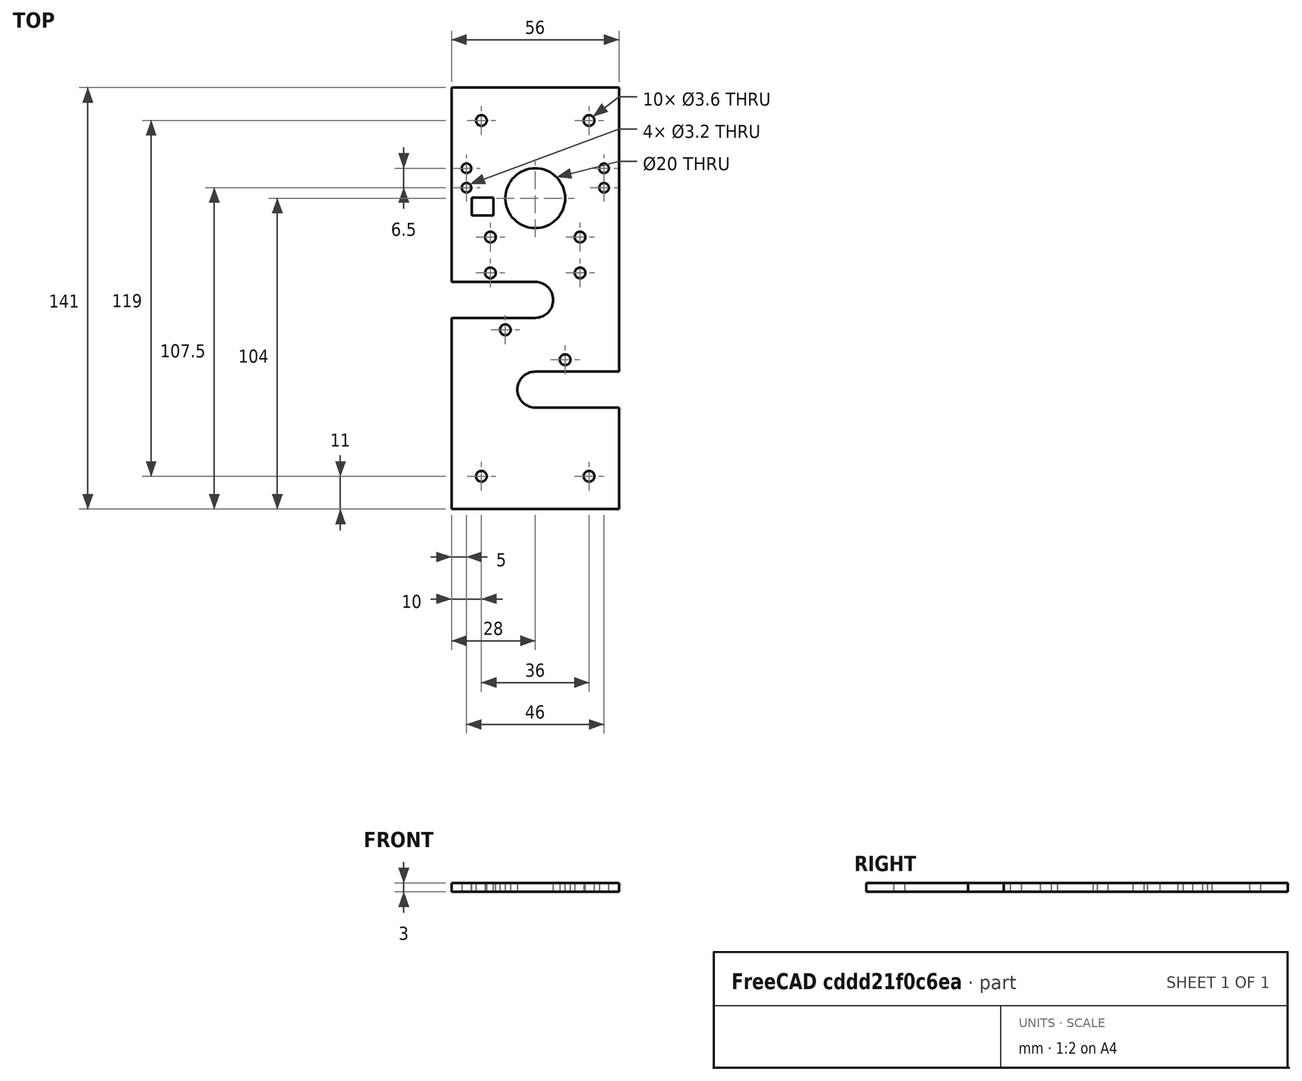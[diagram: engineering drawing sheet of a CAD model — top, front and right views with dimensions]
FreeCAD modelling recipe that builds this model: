
FCSTD DOCUMENT  (FreeCAD 0.16R6706 (Git))
Label: Plate Extrusora
License: All rights reserved
LicenseURL: http://en.wikipedia.org/wiki/All_rights_reserved
objects: Path::FeaturePython×19, Sketcher::SketchObject×1, PartDesign::Pad×1, Path::FeatureCompoundPython×1
note: 3 computed .brp shape members not serialized (recipe doc carries the construction recipe); baked Part::Feature solids carry a one-line shape summary decoded from their .brp

FEATURE [Sketcher::SketchObject] Sketch
  sketch-geometry (40):
    g0: LineSegment StartX=-28 StartY=141 StartZ=0 EndX=28 EndY=141 EndZ=0
    g1: LineSegment StartX=28 StartY=141 StartZ=0 EndX=28 EndY=46 EndZ=0
    g2: LineSegment StartX=28 StartY=0 StartZ=0 EndX=-28 EndY=0 EndZ=0
    g3: LineSegment StartX=-28 StartY=0 StartZ=0 EndX=-28 EndY=64 EndZ=0
    g4: ArcOfCircle CenterX=0 CenterY=70 CenterZ=0 NormalX=0 NormalY=0 NormalZ=1 Radius=6 StartAngle=4.71239 EndAngle=7.85398
    g5: ArcOfCircle CenterX=-1e-12 CenterY=40 CenterZ=0 NormalX=0 NormalY=0 NormalZ=1 Radius=6 StartAngle=1.5708 EndAngle=4.71239
    g6: Circle CenterX=0 CenterY=104 CenterZ=0 NormalX=0 NormalY=0 NormalZ=1 Radius=10
    g7: LineSegment [constr] StartX=-18 StartY=130 StartZ=0 EndX=18 EndY=130 EndZ=0
    g8: Circle CenterX=-18 CenterY=130 CenterZ=0 NormalX=0 NormalY=0 NormalZ=1 Radius=1.8
    g9: Circle CenterX=18 CenterY=130 CenterZ=0 NormalX=0 NormalY=0 NormalZ=1 Radius=1.8
    g10: LineSegment [constr] StartX=-18 StartY=11 StartZ=0 EndX=18 EndY=11 EndZ=0
    g11: Circle CenterX=-18 CenterY=11 CenterZ=0 NormalX=0 NormalY=0 NormalZ=1 Radius=1.8
    g12: Circle CenterX=18 CenterY=11 CenterZ=0 NormalX=0 NormalY=0 NormalZ=1 Radius=1.8
    g13: LineSegment [constr] StartX=-23 StartY=114 StartZ=0 EndX=-23 EndY=107.5 EndZ=0
    g14: Circle CenterX=-23 CenterY=114 CenterZ=0 NormalX=0 NormalY=0 NormalZ=1 Radius=1.6
    g15: Circle CenterX=-23 CenterY=107.5 CenterZ=0 NormalX=0 NormalY=0 NormalZ=1 Radius=1.6
    g16: LineSegment [constr] StartX=23 StartY=114 StartZ=0 EndX=23 EndY=107.5 EndZ=0
    g17: Circle CenterX=23 CenterY=114 CenterZ=0 NormalX=0 NormalY=0 NormalZ=1 Radius=1.6
    g18: Circle CenterX=23 CenterY=107.5 CenterZ=0 NormalX=0 NormalY=0 NormalZ=1 Radius=1.6
    g19: LineSegment [constr] StartX=-24.7268 StartY=119 StartZ=0 EndX=33.9548 EndY=119 EndZ=0
    g20: LineSegment [constr] StartX=-27.9869 StartY=22 StartZ=0 EndX=33.2236 EndY=22 EndZ=0
    g21: LineSegment StartX=-21.2321 StartY=104.225 StartZ=0 EndX=-13.9434 EndY=104.225 EndZ=0
    g22: LineSegment StartX=-13.9434 StartY=104.225 StartZ=0 EndX=-13.9434 EndY=98.2464 EndZ=0
    g23: LineSegment StartX=-13.9434 StartY=98.2464 StartZ=0 EndX=-21.2321 EndY=98.2464 EndZ=0
    g24: LineSegment StartX=-21.2321 StartY=98.2464 StartZ=0 EndX=-21.2321 EndY=104.225 EndZ=0
    g25: LineSegment [constr] StartX=-15 StartY=85 StartZ=0 EndX=15 EndY=85 EndZ=0
    g26: LineSegment StartX=2e-12 StartY=64 StartZ=0 EndX=-28 EndY=64 EndZ=0
    g27: LineSegment StartX=-28 StartY=76 StartZ=0 EndX=3e-12 EndY=76 EndZ=0
    g28: LineSegment StartX=-2e-12 StartY=46 StartZ=0 EndX=28 EndY=46 EndZ=0
    g29: LineSegment StartX=28 StartY=34 StartZ=0 EndX=1e-12 EndY=34 EndZ=0
    g30: LineSegment StartX=28 StartY=34 StartZ=0 EndX=28 EndY=0 EndZ=0
    g31: LineSegment StartX=-28 StartY=76 StartZ=0 EndX=-28 EndY=141 EndZ=0
    g32: Circle CenterX=-10 CenterY=60 CenterZ=0 NormalX=0 NormalY=0 NormalZ=1 Radius=1.8
    g33: Circle CenterX=10 CenterY=50 CenterZ=0 NormalX=0 NormalY=0 NormalZ=1 Radius=1.8
    g34: LineSegment [constr] StartX=-15 StartY=91 StartZ=0 EndX=-15 EndY=79 EndZ=0
    g35: Circle CenterX=-15 CenterY=91 CenterZ=0 NormalX=0 NormalY=0 NormalZ=1 Radius=1.8
    g36: Circle CenterX=-15 CenterY=79 CenterZ=0 NormalX=0 NormalY=0 NormalZ=1 Radius=1.8
    g37: LineSegment [constr] StartX=15 StartY=91 StartZ=0 EndX=15 EndY=79 EndZ=0
    g38: Circle CenterX=15 CenterY=91 CenterZ=0 NormalX=0 NormalY=0 NormalZ=1 Radius=1.8
    g39: Circle CenterX=15 CenterY=79 CenterZ=0 NormalX=0 NormalY=0 NormalZ=1 Radius=1.8
  constraints (109):
    c: Coincident(g0,g1)
    c: Coincident(g30,g2)
    c: Coincident(g2,g3)
    c: Coincident(g31,g0)
    c: Horizontal(g0)
    c: Horizontal(g2)
    c: Vertical(g1)
    c: Vertical(g3)
    c: DistanceY(g30,g1) = 141
    c: DistanceX(g0,g0) = 56
    c: Radius(g6) = 10
    c: Radius(g5) = 6
    c: Equal(g5,g4)
    c: DistanceY(g-1,g5) = 40
    c: DistanceY(g5,g4) = 30
    c: DistanceY(g6,g0) = 37
    c: Horizontal(g7)
    c: DistanceX(g7,g7) = 36
    c: Radius(g8) = 1.8
    c: Equal(g8,g9) = 1.8
    c: Coincident(g7,g8)
    c: Coincident(g7,g9)
    c: DistanceY(g7,g0) = 11
    c: Horizontal(g10)
    c: Equal(g7,g10) = 25
    c: Equal(g8,g11) = 1.8
    c: Equal(g11,g12) = 1.8
    c: Coincident(g10,g12)
    c: DistanceY(g-1,g10) = 11
    c: DistanceY(g13,g13) = 6.5
    c: Vertical(g13)
    c: Radius(g14) = 1.6
    c: Equal(g14,g15) = 1.6
    c: Coincident(g14,g13)
    c: Coincident(g15,g13)
    c: Equal(g13,g16) = 6.5
    c: Vertical(g16)
    c: Equal(g14,g17) = 1.6
    c: Equal(g17,g18) = 1.6
    c: Coincident(g17,g16)
    c: Coincident(g18,g16)
    c: DistanceX(g0,g13) = 5
    c: DistanceX(g16,g0) = 5
    c: Horizontal(g19)
    c: DistanceY(g19,g0) = 22
    c: Symmetric(g30,g2,g-1)
    c: PointOnObject(g6,g-2)
    c: Horizontal(g20)
    c: DistanceY(g30,g20) = 22
    c: Coincident(g21,g22)
    c: Coincident(g22,g23)
    c: Coincident(g23,g24)
    c: Coincident(g24,g21)
    c: Horizontal(g21)
    c: Horizontal(g23)
    c: Vertical(g22)
    c: Vertical(g24)
    c: DistanceY(g16,g19) = 5
    c: DistanceY(g13,g19) = 5
    c: Horizontal(g25)
    c: Symmetric(g25,g25,g-2)
    c: DistanceX(g25,g25) = 30
    c: DistanceY(g25,g6) = 19
    c: DistanceY(g4,g25) = 15
    c: Horizontal(g26)
    c: Horizontal(g27)
    c: Horizontal(g28)
    c: Horizontal(g29)
    c: Coincident(g5,g28)
    c: Coincident(g5,g29)
    c: Tangent(g1,g30)
    c: Coincident(g28,g1)
    c: Coincident(g29,g30)
    c: Symmetric(g26,g27,g4)
    c: Tangent(g3,g31)
    c: Coincident(g27,g31)
    c: Coincident(g26,g3)
    c: Equal(g8,g32) = 1.8
    c: Equal(g8,g33) = 1.8
    c: DistanceX(g5,g33) = 10
    c: DistanceY(g5,g33) = 10
    c: DistanceX(g32,g4) = 10
    c: DistanceY(g32,g4) = 10
    c: Coincident(g4,g27)
    c: Vertical(g34)
    c: DistanceY(g34,g34) = 12
    c: Radius(g35) = 1.8
    c: Equal(g35,g36) = 1.8
    c: Coincident(g34,g35)
    c: Coincident(g34,g36)
    c: Vertical(g37)
    c: Equal(g34,g37) = 15
    c: Equal(g35,g38) = 1.8
    c: Equal(g38,g39) = 1.8
    c: Coincident(g37,g38)
    c: Coincident(g37,g39)
    c: Symmetric(g37,g37,g25)
    c: Symmetric(g34,g34,g25)
    c: DistanceX(g28,g28) = 28
    c: Equal(g28,g26)
    c: Coincident(g4,g26)
    c: DistanceY(g25,g7) = 45
    c: Equal(g28,g29)
    c: Equal(g29,g26)
    c: Equal(g26,g27)
    c: Angle(g5) = 3.14159
    c: Symmetric(g7,g7,g-2)
    c: Coincident(g11,g10)
    c: Symmetric(g10,g10,g-2)
FEATURE [PartDesign::Pad] Pad
  Length = 3
  Length2 = 100
  Sketch = -> Sketch
  Type = 0
FEATURE [Path::FeaturePython] Machine  label="Machine_"  # Path/CAM operation (typed FeaturePython)
  MachineUnits = 0
  X = 0
  X_Max = 0
  X_Min = 0
  Y = 0
  Y_Max = 0
  Y_Min = 0
  Z = 0
  Z_Max = 0
  Z_Min = 0
FEATURE [Path::FeaturePython] Tool  label="Tool1"  # Path/CAM operation (typed FeaturePython)
  SpindleDir = 0
  SpindleSpeed = 0
  ToolNumber = 1
FEATURE [Path::FeaturePython] Profile  label="Berco"  # Path/CAM operation (typed FeaturePython)
  Active = true
  Base = -> Pad
  ClearanceHeight = 3
  Direction = 1
  Edge1 = -> Pad [Edge81]
  EndPoint = (0,0,0)
  ExtendAtEnd = 0
  ExtendAtStart = 0
  FinalDepth = -3.5
  HorizFeed = 127
  LeadInLineLen = 0
  LeadOutLineLen = 0
  OffsetExtra = 0
  PathClosed = true
  RetractHeight = 0
  RollRadius = 0
  SegLen = 0.5
  Side = 1
  StartDepth = 0
  StartPoint = (0,0,0)
  StepDown = 3.5
  ToolNumber = 1
  UseEndPoint = false
  UsePlacements = false
  UseStartDepth = true
  UseStartPoint = false
  VertFeed = 127
FEATURE [Path::FeaturePython] Profile001  label="Berco001"  # Path/CAM operation (typed FeaturePython)
  Active = true
  Base = -> Pad
  ClearanceHeight = 3
  Direction = 1
  Edge1 = -> Pad [Edge78]
  EndPoint = (0,0,0)
  ExtendAtEnd = 0
  ExtendAtStart = 0
  FinalDepth = -3.5
  HorizFeed = 127
  LeadInLineLen = 0
  LeadOutLineLen = 0
  OffsetExtra = 0
  PathClosed = true
  RetractHeight = 0
  RollRadius = 0
  SegLen = 0.5
  Side = 1
  StartDepth = 0
  StartPoint = (0,0,0)
  StepDown = 3.5
  ToolNumber = 1
  UseEndPoint = false
  UsePlacements = false
  UseStartDepth = true
  UseStartPoint = false
  VertFeed = 127
FEATURE [Path::FeaturePython] Profile002  label="Berco002"  # Path/CAM operation (typed FeaturePython)
  Active = true
  Base = -> Pad
  ClearanceHeight = 3
  Direction = 1
  Edge1 = -> Pad [Edge75]
  EndPoint = (0,0,0)
  ExtendAtEnd = 0
  ExtendAtStart = 0
  FinalDepth = -3.5
  HorizFeed = 127
  LeadInLineLen = 0
  LeadOutLineLen = 0
  OffsetExtra = 0
  PathClosed = true
  RetractHeight = 0
  RollRadius = 0
  SegLen = 0.5
  Side = 1
  StartDepth = 0
  StartPoint = (0,0,0)
  StepDown = 3.5
  ToolNumber = 1
  UseEndPoint = false
  UsePlacements = false
  UseStartDepth = true
  UseStartPoint = false
  VertFeed = 127
FEATURE [Path::FeaturePython] Profile003  label="Berco003"  # Path/CAM operation (typed FeaturePython)
  Active = true
  Base = -> Pad
  ClearanceHeight = 3
  Direction = 1
  Edge1 = -> Pad [Edge72]
  EndPoint = (0,0,0)
  ExtendAtEnd = 0
  ExtendAtStart = 0
  FinalDepth = -3.5
  HorizFeed = 127
  LeadInLineLen = 0
  LeadOutLineLen = 0
  OffsetExtra = 0
  PathClosed = true
  RetractHeight = 0
  RollRadius = 0
  SegLen = 0.5
  Side = 1
  StartDepth = 0
  StartPoint = (0,0,0)
  StepDown = 3.5
  ToolNumber = 1
  UseEndPoint = false
  UsePlacements = false
  UseStartDepth = true
  UseStartPoint = false
  VertFeed = 127
FEATURE [Path::FeaturePython] Profile004  label="Enforcador"  # Path/CAM operation (typed FeaturePython)
  Active = true
  Base = -> Pad
  ClearanceHeight = 3
  Direction = 1
  Edge1 = -> Pad [Edge69]
  EndPoint = (0,0,0)
  ExtendAtEnd = 0
  ExtendAtStart = 0
  FinalDepth = -3.5
  HorizFeed = 127
  LeadInLineLen = 0
  LeadOutLineLen = 0
  OffsetExtra = 0
  PathClosed = true
  RetractHeight = 0
  RollRadius = 0
  SegLen = 0.5
  Side = 1
  StartDepth = 0
  StartPoint = (0,0,0)
  StepDown = 3.5
  ToolNumber = 1
  UseEndPoint = false
  UsePlacements = false
  UseStartDepth = true
  UseStartPoint = false
  VertFeed = 127
FEATURE [Path::FeaturePython] Profile005  label="Enforcador001"  # Path/CAM operation (typed FeaturePython)
  Active = true
  Base = -> Pad
  ClearanceHeight = 3
  Direction = 1
  Edge1 = -> Pad [Edge66]
  EndPoint = (0,0,0)
  ExtendAtEnd = 0
  ExtendAtStart = 0
  FinalDepth = -3.5
  HorizFeed = 127
  LeadInLineLen = 0
  LeadOutLineLen = 0
  OffsetExtra = 0
  PathClosed = true
  RetractHeight = 0
  RollRadius = 0
  SegLen = 0.5
  Side = 1
  StartDepth = 0
  StartPoint = (0,0,0)
  StepDown = 3.5
  ToolNumber = 1
  UseEndPoint = false
  UsePlacements = false
  UseStartDepth = true
  UseStartPoint = false
  VertFeed = 127
FEATURE [Path::FeaturePython] Profile006  label="presilha correia"  # Path/CAM operation (typed FeaturePython)
  Active = true
  Base = -> Pad
  ClearanceHeight = 3
  Direction = 1
  Edge1 = -> Pad [Edge60]
  EndPoint = (0,0,0)
  ExtendAtEnd = 0
  ExtendAtStart = 0
  FinalDepth = -3.5
  HorizFeed = 127
  LeadInLineLen = 0
  LeadOutLineLen = 0
  OffsetExtra = 0
  PathClosed = true
  RetractHeight = 0
  RollRadius = 0
  SegLen = 0.5
  Side = 1
  StartDepth = 0
  StartPoint = (0,0,0)
  StepDown = 3.5
  ToolNumber = 1
  UseEndPoint = false
  UsePlacements = false
  UseStartDepth = true
  UseStartPoint = false
  VertFeed = 127
FEATURE [Path::FeaturePython] Profile007  label="presilha correia001"  # Path/CAM operation (typed FeaturePython)
  Active = true
  Base = -> Pad
  ClearanceHeight = 3
  Direction = 1
  Edge1 = -> Pad [Edge63]
  EndPoint = (0,0,0)
  ExtendAtEnd = 0
  ExtendAtStart = 0
  FinalDepth = -3.5
  HorizFeed = 127
  LeadInLineLen = 0
  LeadOutLineLen = 0
  OffsetExtra = 0
  PathClosed = true
  RetractHeight = 0
  RollRadius = 0
  SegLen = 0.5
  Side = 1
  StartDepth = 0
  StartPoint = (0,0,0)
  StepDown = 3.5
  ToolNumber = 1
  UseEndPoint = false
  UsePlacements = false
  UseStartDepth = true
  UseStartPoint = false
  VertFeed = 127
FEATURE [Path::FeaturePython] Profile008  label="presilha correia002"  # Path/CAM operation (typed FeaturePython)
  Active = true
  Base = -> Pad
  ClearanceHeight = 3
  Direction = 1
  Edge1 = -> Pad [Edge54]
  EndPoint = (0,0,0)
  ExtendAtEnd = 0
  ExtendAtStart = 0
  FinalDepth = -3.5
  HorizFeed = 127
  LeadInLineLen = 0
  LeadOutLineLen = 0
  OffsetExtra = 0
  PathClosed = true
  RetractHeight = 0
  RollRadius = 0
  SegLen = 0.5
  Side = 1
  StartDepth = 0
  StartPoint = (0,0,0)
  StepDown = 3.5
  ToolNumber = 1
  UseEndPoint = false
  UsePlacements = false
  UseStartDepth = true
  UseStartPoint = false
  VertFeed = 127
FEATURE [Path::FeaturePython] Profile009  label="presilha correia003"  # Path/CAM operation (typed FeaturePython)
  Active = true
  Base = -> Pad
  ClearanceHeight = 3
  Direction = 1
  Edge1 = -> Pad [Edge57]
  EndPoint = (0,0,0)
  ExtendAtEnd = 0
  ExtendAtStart = 0
  FinalDepth = -3.5
  HorizFeed = 127
  LeadInLineLen = 0
  LeadOutLineLen = 0
  OffsetExtra = 0
  PathClosed = true
  RetractHeight = 0
  RollRadius = 0
  SegLen = 0.5
  Side = 1
  StartDepth = 0
  StartPoint = (0,0,0)
  StepDown = 3.5
  ToolNumber = 1
  UseEndPoint = false
  UsePlacements = false
  UseStartDepth = true
  UseStartPoint = false
  VertFeed = 127
FEATURE [Path::FeaturePython] Profile010  label="pass cabos"  # Path/CAM operation (typed FeaturePython)
  Active = true
  Base = -> Pad
  ClearanceHeight = 3
  Direction = 1
  Edge1 = -> Pad [Edge49]
  Edge2 = -> Pad [Edge51]
  EndPoint = (0,0,0)
  ExtendAtEnd = 0
  ExtendAtStart = 0
  FinalDepth = -3.5
  HorizFeed = 127
  LeadInLineLen = 0
  LeadOutLineLen = 0
  OffsetExtra = 0
  PathClosed = true
  RetractHeight = 0
  RollRadius = 0
  SegLen = 0.5
  Side = 1
  StartDepth = 0
  StartPoint = (0,0,0)
  StepDown = 3.5
  ToolNumber = 1
  UseEndPoint = false
  UsePlacements = false
  UseStartDepth = true
  UseStartPoint = false
  VertFeed = 127
FEATURE [Path::FeaturePython] Profile011  label="endstop"  # Path/CAM operation (typed FeaturePython)
  Active = true
  Base = -> Pad
  ClearanceHeight = 3
  Direction = 1
  Edge1 = -> Pad [Edge90]
  EndPoint = (0,0,0)
  ExtendAtEnd = 0
  ExtendAtStart = 0
  FinalDepth = -3.5
  HorizFeed = 127
  LeadInLineLen = 0
  LeadOutLineLen = 0
  OffsetExtra = 0
  PathClosed = true
  RetractHeight = 0
  RollRadius = 0
  SegLen = 0.5
  Side = 1
  StartDepth = 0
  StartPoint = (0,0,0)
  StepDown = 3.5
  ToolNumber = 1
  UseEndPoint = false
  UsePlacements = false
  UseStartDepth = true
  UseStartPoint = false
  VertFeed = 127
FEATURE [Path::FeaturePython] Profile012  label="endstop001"  # Path/CAM operation (typed FeaturePython)
  Active = true
  Base = -> Pad
  ClearanceHeight = 3
  Direction = 1
  Edge1 = -> Pad [Edge93]
  EndPoint = (0,0,0)
  ExtendAtEnd = 0
  ExtendAtStart = 0
  FinalDepth = -3.5
  HorizFeed = 127
  LeadInLineLen = 0
  LeadOutLineLen = 0
  OffsetExtra = 0
  PathClosed = true
  RetractHeight = 0
  RollRadius = 0
  SegLen = 0.5
  Side = 1
  StartDepth = 0
  StartPoint = (0,0,0)
  StepDown = 3.5
  ToolNumber = 1
  UseEndPoint = false
  UsePlacements = false
  UseStartDepth = true
  UseStartPoint = false
  VertFeed = 127
FEATURE [Path::FeaturePython] Profile013  label="endstop002"  # Path/CAM operation (typed FeaturePython)
  Active = true
  Base = -> Pad
  ClearanceHeight = 3
  Direction = 1
  Edge1 = -> Pad [Edge84]
  EndPoint = (0,0,0)
  ExtendAtEnd = 0
  ExtendAtStart = 0
  FinalDepth = -3.5
  HorizFeed = 127
  LeadInLineLen = 0
  LeadOutLineLen = 0
  OffsetExtra = 0
  PathClosed = true
  RetractHeight = 0
  RollRadius = 0
  SegLen = 0.5
  Side = 1
  StartDepth = 0
  StartPoint = (0,0,0)
  StepDown = 3.5
  ToolNumber = 1
  UseEndPoint = false
  UsePlacements = false
  UseStartDepth = true
  UseStartPoint = false
  VertFeed = 127
FEATURE [Path::FeaturePython] Profile014  label="endstop003"  # Path/CAM operation (typed FeaturePython)
  Active = true
  Base = -> Pad
  ClearanceHeight = 3
  Direction = 1
  Edge1 = -> Pad [Edge87]
  EndPoint = (0,0,0)
  ExtendAtEnd = 0
  ExtendAtStart = 0
  FinalDepth = -3.5
  HorizFeed = 127
  LeadInLineLen = 0
  LeadOutLineLen = 0
  OffsetExtra = 0
  PathClosed = true
  RetractHeight = 0
  RollRadius = 0
  SegLen = 0.5
  Side = 1
  StartDepth = 0
  StartPoint = (0,0,0)
  StepDown = 3.5
  ToolNumber = 1
  UseEndPoint = false
  UsePlacements = false
  UseStartDepth = true
  UseStartPoint = false
  VertFeed = 127
FEATURE [Path::FeaturePython] Profile015  label="sensor capacitivo"  # Path/CAM operation (typed FeaturePython)
  Active = true
  Base = -> Pad
  ClearanceHeight = 3
  Direction = 1
  Edge1 = -> Pad [Edge39]
  EndPoint = (0,0,0)
  ExtendAtEnd = 0
  ExtendAtStart = 0
  FinalDepth = -3.5
  HorizFeed = 127
  LeadInLineLen = 0
  LeadOutLineLen = 0
  OffsetExtra = 0
  PathClosed = true
  RetractHeight = 0
  RollRadius = 0
  SegLen = 0.5
  Side = 1
  StartDepth = 0
  StartPoint = (0,0,0)
  StepDown = 3.5
  ToolNumber = 1
  UseEndPoint = false
  UsePlacements = false
  UseStartDepth = true
  UseStartPoint = false
  VertFeed = 127
FEATURE [Path::FeaturePython] Profile016  label="Externo"  # Path/CAM operation (typed FeaturePython)
  Active = true
  Base = -> Pad
  ClearanceHeight = 3
  Direction = 0
  EndPoint = (0,0,0)
  ExtendAtEnd = 0
  ExtendAtStart = 0
  Face1 = -> Pad [Face33]
  FinalDepth = -3.5
  HorizFeed = 127
  LeadInLineLen = 0
  LeadOutLineLen = 0
  OffsetExtra = 0
  PathClosed = true
  RetractHeight = 0
  RollRadius = 0
  SegLen = 0.5
  Side = 0
  StartDepth = 0
  StartPoint = (0,0,0)
  StepDown = 3.5
  ToolNumber = 1
  UseEndPoint = false
  UsePlacements = false
  UseStartDepth = true
  UseStartPoint = false
  VertFeed = 127
FEATURE [Path::FeatureCompoundPython] Project  # Path/CAM operation (typed FeaturePython)
  Group = -> [Machine,Tool,Profile,Profile001,Profile002,Profile003,Profile004,Profile005,Profile006,Profile007,Profile008,Profile009,Profile010,Profile011,Profile012,Profile013,Profile014,Profile015,Profile016]
  UsePlacements = false
